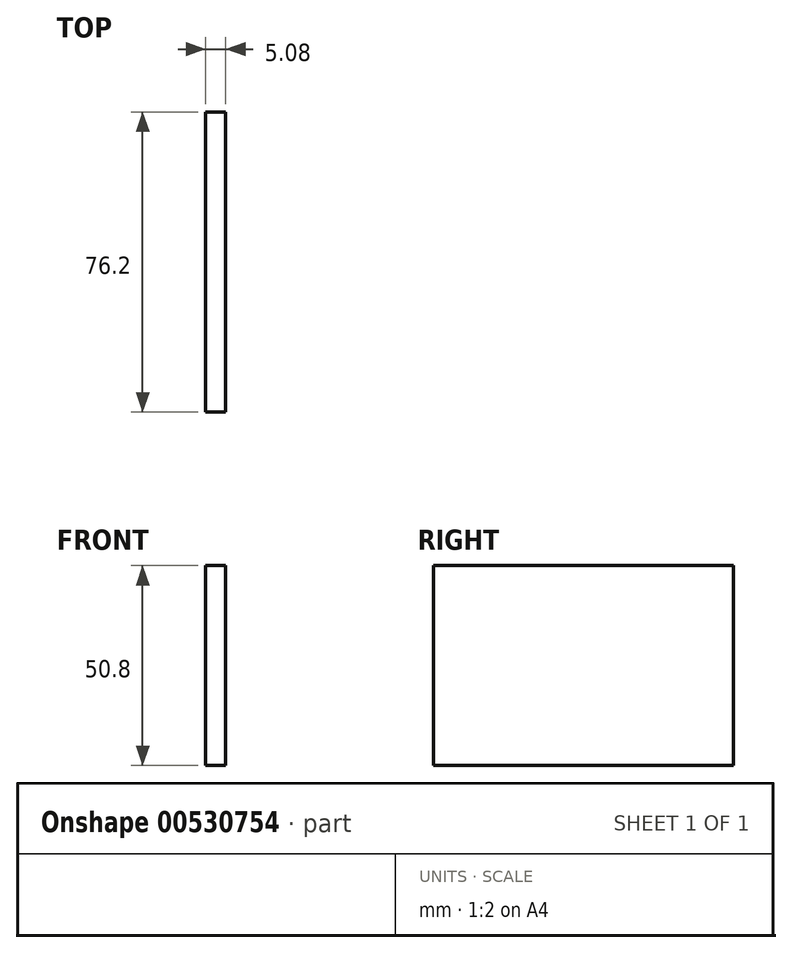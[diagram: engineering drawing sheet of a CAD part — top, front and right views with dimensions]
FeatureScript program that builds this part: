
annotation { "Feature Type Name" : "Feature", "Feature Type Description" : "" }
export const myFeature = defineFeature(function(context is Context, id is Id, definition is map)
    precondition{}
    {
        {
            var Q0;
            Q0=qCreatedBy(makeId("Right.planeOp"),FACE);
            var sketch = newSketch(context, id + "F0", { "sketchPlane" : qUnion([Q0])});
            skLineSegment(sketch, "E0", {"start": v(-35.58, 35.05) * mm, "end": v(40.62, 35.05) * mm});
            skLineSegment(sketch, "E1", {"start": v(40.62, 35.05) * mm, "end": v(40.62, -15.75) * mm});
            skLineSegment(sketch, "E2", {"start": v(40.62, -15.75) * mm, "end": v(-35.58, -15.75) * mm});
            skLineSegment(sketch, "E3", {"start": v(-35.58, -15.75) * mm, "end": v(-35.58, 35.05) * mm});
            skSolve(sketch);
        }
        {
            var Q0;
            Q0=sQuery(id+"F0.wireOp",EDGE,"E0");
            var Q1;
            Q1=sQuery(id+"F0.wireOp",EDGE,"E2");
            extrude(context, id + "F1", {"bodyType" : ToolBodyType.SURFACE, "surfaceEntities" : qUnion([Q0, Q1]), "depth" : 12.7 * mm, "offsetDistance" : 25.4 * mm});
        }
        {
            var Q0;
            Q0=sQuery(id+"F0.wireOp",EDGE,"E1");
            extrude(context, id + "F2", {"bodyType" : ToolBodyType.SURFACE, "surfaceEntities" : qUnion([Q0]), "depth" : 12.7 * mm, "offsetDistance" : 25.4 * mm});
        }
        {
            var Q0;
            Q0=makeQuery(id+"F0.imprint","IMPRINT",FACE,{"disambiguationData":[TD([[makeQuery(id+"F0.imprint","IMPRINT",EDGE,{"derivedFrom":sQuery(id+"F0.wireOp",EDGE,"E0")}),-1.0]])]});
            extrude(context, id + "F3", {"entities" : qUnion([Q0]), "depth" : -5.08 * mm, "offsetDistance" : 25.4 * mm});
        }
    });
